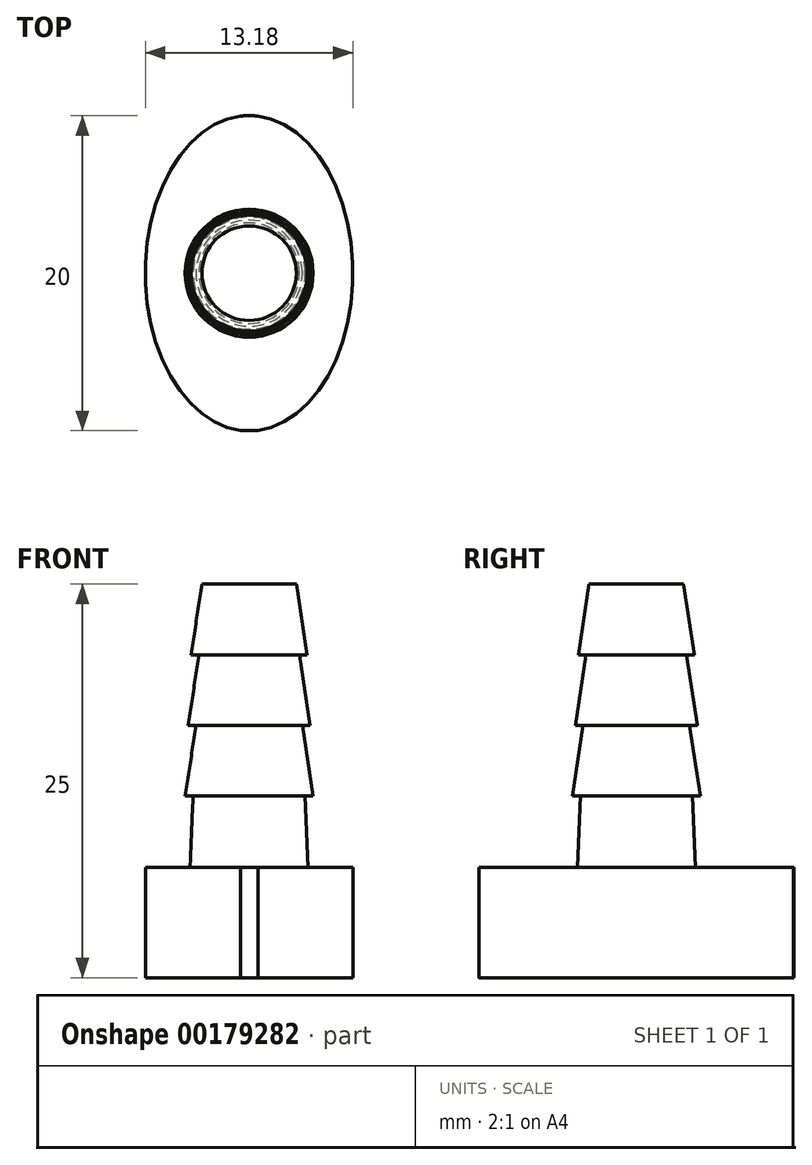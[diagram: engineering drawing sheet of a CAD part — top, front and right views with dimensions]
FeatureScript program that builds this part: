
annotation { "Feature Type Name" : "Feature", "Feature Type Description" : "" }
export const myFeature = defineFeature(function(context is Context, id is Id, definition is map)
    precondition{}
    {
        {
            var Q0;
            Q0=qCreatedBy(makeId("Right.planeOp"),FACE);
            var sketch = newSketch(context, id + "F0", { "sketchPlane" : qUnion([Q0])});
            skLineSegment(sketch, "E0", {"start": v(0, 0) * mm, "end": v(0, 62.3) * mm, "construction": true});
            skLineSegment(sketch, "E1", {"start": v(0, 25) * mm, "end": v(3, 25) * mm});
            skLineSegment(sketch, "E2", {"start": v(3, 25) * mm, "end": v(3.75, 7) * mm, "construction": true});
            skLineSegment(sketch, "E3", {"start": v(3.75, 7) * mm, "end": v(10, 7) * mm});
            skLineSegment(sketch, "E4", {"start": v(10, 7) * mm, "end": v(10, 0) * mm});
            skLineSegment(sketch, "E5", {"start": v(10, 0) * mm, "end": v(0, 0) * mm});
            skLineSegment(sketch, "E6", {"start": v(0, 25) * mm, "end": v(0, 0) * mm});
            skLineSegment(sketch, "E7", {"start": v(3, 25) * mm, "end": v(3.69, 20.51) * mm});
            skLineSegment(sketch, "E8", {"start": v(3.69, 20.51) * mm, "end": v(3.19, 20.51) * mm});
            skLineSegment(sketch, "E9", {"start": v(3.19, 20.51) * mm, "end": v(3.87, 16.02) * mm});
            skLineSegment(sketch, "E10", {"start": v(3.87, 16.02) * mm, "end": v(3.37, 16.02) * mm});
            skLineSegment(sketch, "E11", {"start": v(3.37, 16.02) * mm, "end": v(4.06, 11.54) * mm});
            skLineSegment(sketch, "E12", {"start": v(4.06, 11.54) * mm, "end": v(3.56, 11.54) * mm});
            skLineSegment(sketch, "E13", {"start": v(3.56, 11.54) * mm, "end": v(3.75, 7) * mm});
            skSolve(sketch);
        }
        {
            var Q0;
            Q0 = qSketchRegion(id + "F0", true);
            var Q1;
            Q1=sQuery(id+"F0.wireOp",EDGE,"E0");
            revolve(context, id + "F1", {"surfaceOperationType" : NewSurfaceOperationType.NEW, "entities" : qUnion([Q0]), "axis" : qUnion([Q1]), "revolveType" : RevolveType.FULL});
        }
        {
            var Q0;
            Q0=makeQuery(id+"F1.opRevolve","SWEPT_FACE",FACE,{"disambiguationData":[OSD([sQuery(id+"F0.wireOp",EDGE,"E5")])]});
            var sketch = newSketch(context, id + "F2", { "sketchPlane" : qUnion([Q0])});
            skCircle(sketch, "E14.0", {"center": v(0, 0) * mm, "radius": 10 * mm});
            skEllipse(sketch, "E15", {"center": v(0, 0) * mm, "majorRadius": 10.02 * mm, "minorRadius": 6.6 * mm, "majorAxis": v(0, -1)});
            skSolve(sketch);
        }
        {
            var Q0;
            {var subQ0=sQuery(id+"F2.wireOp",EDGE,"E15");var subQ1=sQuery(id+"F2.wireOp",EDGE,"E14.0");var subQ2=makeQuery(id+"F2.imprint","INTERSECT",VERTEX,{"disambiguationData":[OD(0.0)],"derivedFrom":[subQ1,subQ0]});Q0=makeQuery(id+"F2.imprint","IMPRINT",FACE,{"disambiguationData":[TD([[makeQuery(id+"F2.imprint","IMPRINT",EDGE,{"disambiguationData":[TD([[subQ2,1.0]])],"derivedFrom":subQ1}),1.0]])]});}
            extrude(context, id + "F3", {"entities" : qUnion([Q0]), "operationType" : NewBodyOperationType.INTERSECT, "endBound" : BoundingType.THROUGH_ALL, "oppositeDirection" : true, "depth" : 25 * mm, "offsetDistance" : 25 * mm});
        }
    });
